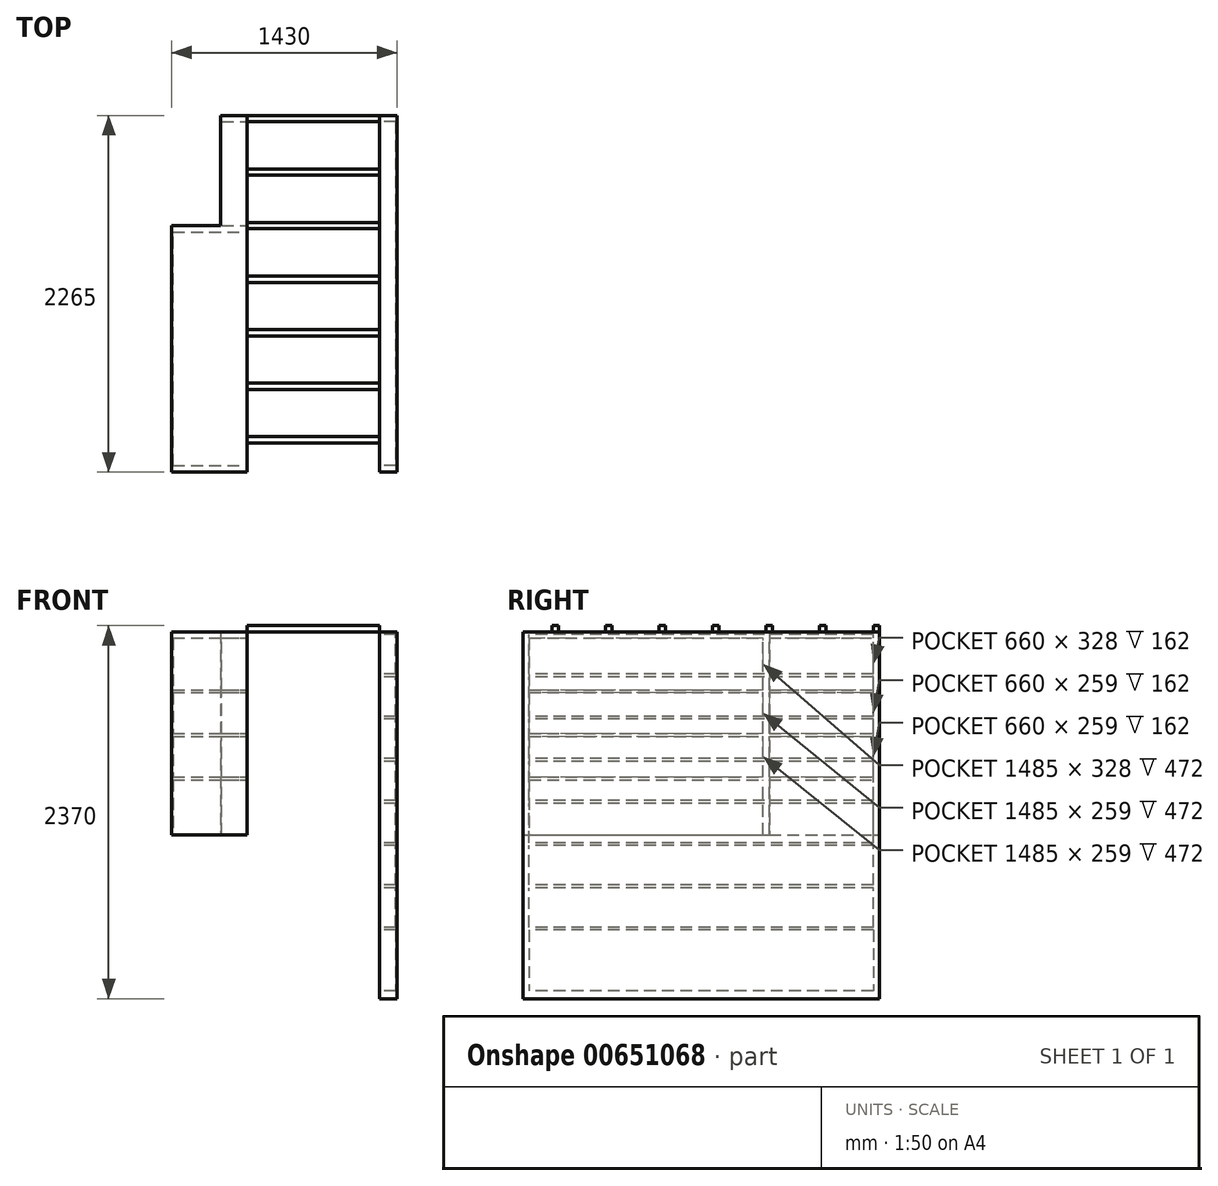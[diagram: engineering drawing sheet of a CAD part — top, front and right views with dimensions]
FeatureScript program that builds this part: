
annotation { "Feature Type Name" : "Feature", "Feature Type Description" : "" }
export const myFeature = defineFeature(function(context is Context, id is Id, definition is map)
    precondition{}
    {
        {
            var Q0;
            Q0=qCreatedBy(makeId("Top.planeOp"),FACE);
            var sketch = newSketch(context, id + "F0", { "sketchPlane" : qUnion([Q0])});
            skLineSegment(sketch, "E0.bottom", {"start": v(0, 0) * mm, "end": v(-110, 0) * mm});
            skLineSegment(sketch, "E0.left", {"start": v(0, 0) * mm, "end": v(0, 789.64) * mm});
            skLineSegment(sketch, "E0.right", {"start": v(-110, 0) * mm, "end": v(-110, 789.64) * mm});
            skLineSegment(sketch, "E1.bottom", {"start": v(-1120, 2265) * mm, "end": v(-950, 2265) * mm});
            skLineSegment(sketch, "E1.top", {"start": v(-1120, 0) * mm, "end": v(-950, 0) * mm});
            skLineSegment(sketch, "E1.left", {"start": v(-1120, 2265) * mm, "end": v(-1120, 1565) * mm});
            skLineSegment(sketch, "E1.right", {"start": v(-950, 2265) * mm, "end": v(-950, 0) * mm});
            skLineSegment(sketch, "E2.bottom", {"start": v(-1120, 1565) * mm, "end": v(-1430, 1565) * mm});
            skLineSegment(sketch, "E2.top", {"start": v(-950, 0) * mm, "end": v(-1430, 0) * mm});
            skLineSegment(sketch, "E2.right", {"start": v(-1430, 1565) * mm, "end": v(-1430, 0) * mm});
            skLineSegment(sketch, "E3.bottom", {"start": v(-110, 2265) * mm, "end": v(0, 2265) * mm});
            skLineSegment(sketch, "E3.top", {"start": v(-110, 0) * mm, "end": v(0, 0) * mm});
            skLineSegment(sketch, "E3.left", {"start": v(-110, 2265) * mm, "end": v(-110, 0) * mm});
            skLineSegment(sketch, "E3.right", {"start": v(0, 2265) * mm, "end": v(0, 0) * mm});
            skSolve(sketch);
        }
        {
            var Q0;
            Q0=qSketchRegion(id+"F0",true);
            extrude(context, id + "F1", {"entities" : qUnion([Q0]), "depth" : 2330 * mm, "offsetDistance" : 25 * mm});
        }
        {
            var Q0;
            Q0=makeQuery(id+"F1.opExtrude","SWEPT_FACE",FACE,{"disambiguationData":[OSD([sQuery(id+"F0.wireOp",EDGE,"E3.left")])]});
            var sketch = newSketch(context, id + "F2", { "sketchPlane" : qUnion([Q0])});
            skLineSegment(sketch, "E4.0", {"start": v(-2265, 2330) * mm, "end": v(-2265, 0) * mm});
            skLineSegment(sketch, "E5.0", {"start": v(0, 2330) * mm, "end": v(0, 0) * mm});
            skLineSegment(sketch, "E6.0", {"start": v(-2265, 2330) * mm, "end": v(0, 2330) * mm});
            skLineSegment(sketch, "E7.0", {"start": v(-2265, 0) * mm, "end": v(0, 0) * mm});
            skLineSegment(sketch, "E8.bottom", {"start": v(-2225, 436) * mm, "end": v(-40, 436) * mm});
            skLineSegment(sketch, "E8.top", {"start": v(-2225, 50) * mm, "end": v(-40, 50) * mm});
            skLineSegment(sketch, "E8.left", {"start": v(-2225, 436) * mm, "end": v(-2225, 50) * mm});
            skLineSegment(sketch, "E8.right", {"start": v(-40, 436) * mm, "end": v(-40, 50) * mm});
            skLineSegment(sketch, "E9.bottom", {"start": v(-2225, 454) * mm, "end": v(-40, 454) * mm});
            skLineSegment(sketch, "E9.top", {"start": v(-2225, 704) * mm, "end": v(-40, 704) * mm});
            skLineSegment(sketch, "E9.left", {"start": v(-2225, 454) * mm, "end": v(-2225, 704) * mm});
            skLineSegment(sketch, "E9.right", {"start": v(-40, 454) * mm, "end": v(-40, 704) * mm});
            skLineSegment(sketch, "E10.bottom", {"start": v(-2225, 722) * mm, "end": v(-40, 722) * mm});
            skLineSegment(sketch, "E10.top", {"start": v(-2225, 972) * mm, "end": v(-40, 972) * mm});
            skLineSegment(sketch, "E10.left", {"start": v(-2225, 722) * mm, "end": v(-2225, 972) * mm});
            skLineSegment(sketch, "E10.right", {"start": v(-40, 722) * mm, "end": v(-40, 972) * mm});
            skLineSegment(sketch, "E11.bottom", {"start": v(-2225, 990) * mm, "end": v(-40, 990) * mm});
            skLineSegment(sketch, "E11.top", {"start": v(-2225, 1240) * mm, "end": v(-40, 1240) * mm});
            skLineSegment(sketch, "E11.left", {"start": v(-2225, 990) * mm, "end": v(-2225, 1240) * mm});
            skLineSegment(sketch, "E11.right", {"start": v(-40, 990) * mm, "end": v(-40, 1240) * mm});
            skLineSegment(sketch, "E12.bottom", {"start": v(-2225, 1258) * mm, "end": v(-40, 1258) * mm});
            skLineSegment(sketch, "E12.top", {"start": v(-2225, 1508) * mm, "end": v(-40, 1508) * mm});
            skLineSegment(sketch, "E12.left", {"start": v(-2225, 1258) * mm, "end": v(-2225, 1508) * mm});
            skLineSegment(sketch, "E12.right", {"start": v(-40, 1258) * mm, "end": v(-40, 1508) * mm});
            skLineSegment(sketch, "E13.bottom", {"start": v(-2225, 1526) * mm, "end": v(-40, 1526) * mm});
            skLineSegment(sketch, "E13.top", {"start": v(-2225, 1776) * mm, "end": v(-40, 1776) * mm});
            skLineSegment(sketch, "E13.left", {"start": v(-2225, 1526) * mm, "end": v(-2225, 1776) * mm});
            skLineSegment(sketch, "E13.right", {"start": v(-40, 1526) * mm, "end": v(-40, 1776) * mm});
            skLineSegment(sketch, "E14.bottom", {"start": v(-2225, 1794) * mm, "end": v(-40, 1794) * mm});
            skLineSegment(sketch, "E14.top", {"start": v(-2225, 2044) * mm, "end": v(-40, 2044) * mm});
            skLineSegment(sketch, "E14.left", {"start": v(-2225, 1794) * mm, "end": v(-2225, 2044) * mm});
            skLineSegment(sketch, "E14.right", {"start": v(-40, 1794) * mm, "end": v(-40, 2044) * mm});
            skLineSegment(sketch, "E15.bottom", {"start": v(-2225, 2062) * mm, "end": v(-40, 2062) * mm});
            skLineSegment(sketch, "E15.top", {"start": v(-2225, 2312) * mm, "end": v(-40, 2312) * mm});
            skLineSegment(sketch, "E15.left", {"start": v(-2225, 2062) * mm, "end": v(-2225, 2312) * mm});
            skLineSegment(sketch, "E15.right", {"start": v(-40, 2062) * mm, "end": v(-40, 2312) * mm});
            skSolve(sketch);
        }
        {
            var Q0;
            Q0=makeQuery(id+"F2.imprint","IMPRINT",FACE,{"disambiguationData":[TD([[makeQuery(id+"F2.imprint","IMPRINT",EDGE,{"derivedFrom":sQuery(id+"F2.wireOp",EDGE,"E15.bottom")}),1.0]])]});
            var Q1;
            Q1=makeQuery(id+"F2.imprint","IMPRINT",FACE,{"disambiguationData":[TD([[makeQuery(id+"F2.imprint","IMPRINT",EDGE,{"derivedFrom":sQuery(id+"F2.wireOp",EDGE,"E14.bottom")}),1.0]])]});
            var Q2;
            Q2=makeQuery(id+"F2.imprint","IMPRINT",FACE,{"disambiguationData":[TD([[makeQuery(id+"F2.imprint","IMPRINT",EDGE,{"derivedFrom":sQuery(id+"F2.wireOp",EDGE,"E13.bottom")}),1.0]])]});
            var Q3;
            Q3=makeQuery(id+"F2.imprint","IMPRINT",FACE,{"disambiguationData":[TD([[makeQuery(id+"F2.imprint","IMPRINT",EDGE,{"derivedFrom":sQuery(id+"F2.wireOp",EDGE,"E12.bottom")}),1.0]])]});
            var Q4;
            Q4=makeQuery(id+"F2.imprint","IMPRINT",FACE,{"disambiguationData":[TD([[makeQuery(id+"F2.imprint","IMPRINT",EDGE,{"derivedFrom":sQuery(id+"F2.wireOp",EDGE,"E11.bottom")}),1.0]])]});
            var Q5;
            Q5=makeQuery(id+"F2.imprint","IMPRINT",FACE,{"disambiguationData":[TD([[makeQuery(id+"F2.imprint","IMPRINT",EDGE,{"derivedFrom":sQuery(id+"F2.wireOp",EDGE,"E10.bottom")}),1.0]])]});
            var Q6;
            Q6=makeQuery(id+"F2.imprint","IMPRINT",FACE,{"disambiguationData":[TD([[makeQuery(id+"F2.imprint","IMPRINT",EDGE,{"derivedFrom":sQuery(id+"F2.wireOp",EDGE,"E9.bottom")}),1.0]])]});
            var Q7;
            Q7=makeQuery(id+"F2.imprint","IMPRINT",FACE,{"disambiguationData":[TD([[makeQuery(id+"F2.imprint","IMPRINT",EDGE,{"derivedFrom":sQuery(id+"F2.wireOp",EDGE,"E8.bottom")}),-1.0]])]});
            extrude(context, id + "F3", {"entities" : qUnion([Q0, Q1, Q2, Q3, Q4, Q5, Q6, Q7]), "operationType" : NewBodyOperationType.REMOVE, "oppositeDirection" : true, "depth" : 102 * mm, "offsetDistance" : 25 * mm});
        }
        {
            var Q0;
            Q0=makeQuery(id+"F1.opExtrude","SWEPT_FACE",FACE,{"disambiguationData":[OSD([sQuery(id+"F0.wireOp",EDGE,"E1.right")])]});
            var sketch = newSketch(context, id + "F4", { "sketchPlane" : qUnion([Q0])});
            skLineSegment(sketch, "E16.0", {"start": v(0, 2330) * mm, "end": v(0, 0) * mm});
            skLineSegment(sketch, "E17.0.1", {"start": v(0, 0) * mm, "end": v(1565, 0) * mm});
            skLineSegment(sketch, "E17.0.3", {"start": v(1565, 0) * mm, "end": v(2265, 0) * mm});
            skLineSegment(sketch, "E17.0.5", {"start": v(2265, 0) * mm, "end": v(0, 0) * mm});
            skLineSegment(sketch, "E18.0", {"start": v(2265, 2330) * mm, "end": v(2265, 0) * mm});
            skLineSegment(sketch, "E19.bottom", {"start": v(0, 0) * mm, "end": v(2265, 0) * mm});
            skLineSegment(sketch, "E19.top", {"start": v(0, 1040) * mm, "end": v(2265, 1040) * mm});
            skLineSegment(sketch, "E19.left", {"start": v(0, 0) * mm, "end": v(0, 1040) * mm});
            skLineSegment(sketch, "E19.right", {"start": v(2265, 0) * mm, "end": v(2265, 1040) * mm});
            skSolve(sketch);
        }
        {
            var Q0;
            Q0=qSketchRegion(id+"F4",true);
            extrude(context, id + "F5", {"entities" : qUnion([Q0]), "operationType" : NewBodyOperationType.REMOVE, "oppositeDirection" : true, "depth" : 480 * mm, "offsetDistance" : 25 * mm});
        }
        {
            var Q0;
            Q0=makeQuery(id+"F1.opExtrude","SWEPT_FACE",FACE,{"disambiguationData":[OSD([sQuery(id+"F0.wireOp",EDGE,"E1.right")])]});
            var sketch = newSketch(context, id + "F6", { "sketchPlane" : qUnion([Q0])});
            skLineSegment(sketch, "E20.0", {"start": v(0, 2330) * mm, "end": v(0, 1040) * mm});
            skLineSegment(sketch, "E21.0", {"start": v(0, 1040) * mm, "end": v(2265, 1040) * mm});
            skLineSegment(sketch, "E22.0", {"start": v(2265, 2330) * mm, "end": v(2265, 1040) * mm});
            skLineSegment(sketch, "E23.bottom", {"start": v(2265, 1040) * mm, "end": v(2225, 1040) * mm});
            skLineSegment(sketch, "E23.top", {"start": v(2265, 2330) * mm, "end": v(2225, 2330) * mm});
            skLineSegment(sketch, "E23.left", {"start": v(2265, 1040) * mm, "end": v(2265, 2330) * mm});
            skLineSegment(sketch, "E23.right", {"start": v(2225, 1040) * mm, "end": v(2225, 2330) * mm});
            skLineSegment(sketch, "E24.bottom", {"start": v(0, 2290) * mm, "end": v(2225, 2290) * mm});
            skLineSegment(sketch, "E24.top", {"start": v(0, 2330) * mm, "end": v(2225, 2330) * mm});
            skLineSegment(sketch, "E24.left", {"start": v(0, 2290) * mm, "end": v(0, 2330) * mm});
            skLineSegment(sketch, "E24.right", {"start": v(2225, 2290) * mm, "end": v(2225, 2330) * mm});
            skLineSegment(sketch, "E25.bottom", {"start": v(0, 2290) * mm, "end": v(40, 2290) * mm});
            skLineSegment(sketch, "E25.top", {"start": v(0, 1040) * mm, "end": v(40, 1040) * mm});
            skLineSegment(sketch, "E25.left", {"start": v(0, 2290) * mm, "end": v(0, 1040) * mm});
            skLineSegment(sketch, "E25.right", {"start": v(40, 2290) * mm, "end": v(40, 1040) * mm});
            skLineSegment(sketch, "E26.bottom", {"start": v(1565, 1040) * mm, "end": v(1525, 1040) * mm});
            skLineSegment(sketch, "E26.top", {"start": v(1565, 2290) * mm, "end": v(1525, 2290) * mm});
            skLineSegment(sketch, "E26.left", {"start": v(1565, 1040) * mm, "end": v(1565, 2290) * mm});
            skLineSegment(sketch, "E26.right", {"start": v(1525, 1040) * mm, "end": v(1525, 2290) * mm});
            skLineSegment(sketch, "E27.bottom", {"start": v(40, 1390) * mm, "end": v(2225, 1390) * mm});
            skLineSegment(sketch, "E27.top", {"start": v(40, 1408) * mm, "end": v(2225, 1408) * mm});
            skLineSegment(sketch, "E27.left", {"start": v(40, 1390) * mm, "end": v(40, 1408) * mm});
            skLineSegment(sketch, "E27.right", {"start": v(2225, 1390) * mm, "end": v(2225, 1408) * mm});
            skLineSegment(sketch, "E28.bottom", {"start": v(40, 1667) * mm, "end": v(2225, 1667) * mm});
            skLineSegment(sketch, "E28.top", {"start": v(40, 1685) * mm, "end": v(2225, 1685) * mm});
            skLineSegment(sketch, "E28.left", {"start": v(40, 1667) * mm, "end": v(40, 1685) * mm});
            skLineSegment(sketch, "E28.right", {"start": v(2225, 1667) * mm, "end": v(2225, 1685) * mm});
            skLineSegment(sketch, "E29.bottom", {"start": v(40, 1944) * mm, "end": v(2225, 1944) * mm});
            skLineSegment(sketch, "E29.top", {"start": v(40, 1962) * mm, "end": v(2225, 1962) * mm});
            skLineSegment(sketch, "E29.left", {"start": v(40, 1944) * mm, "end": v(40, 1962) * mm});
            skLineSegment(sketch, "E29.right", {"start": v(2225, 1944) * mm, "end": v(2225, 1962) * mm});
            skSolve(sketch);
        }
        {
            var Q0;
            {var subQ3=sQuery(id+"F6.wireOp",EDGE,"E26.left");var subQ5=sQuery(id+"F6.wireOp",EDGE,"E27.bottom");var subQ7=makeQuery(id+"F6.imprint","INTERSECT",VERTEX,{"derivedFrom":[subQ3,subQ5]});Q0=makeQuery(id+"F6.imprint","IMPRINT",FACE,{"disambiguationData":[TD([[makeQuery(id+"F6.imprint","IMPRINT",EDGE,{"disambiguationData":[TD([[subQ7,1.0]])],"derivedFrom":subQ3}),-1.0]])]});}
            var Q1;
            {var subQ0=sQuery(id+"F6.wireOp",EDGE,"E27.top");var subQ5=sQuery(id+"F6.wireOp",EDGE,"E26.left");var subQ6=makeQuery(id+"F6.imprint","INTERSECT",VERTEX,{"derivedFrom":[subQ5,subQ0]});Q1=makeQuery(id+"F6.imprint","IMPRINT",FACE,{"disambiguationData":[TD([[makeQuery(id+"F6.imprint","IMPRINT",EDGE,{"disambiguationData":[TD([[subQ6,-1.0]])],"derivedFrom":subQ5}),-1.0]])]});}
            var Q2;
            {var subQ0=sQuery(id+"F6.wireOp",EDGE,"E28.top");var subQ5=sQuery(id+"F6.wireOp",EDGE,"E26.left");var subQ6=makeQuery(id+"F6.imprint","INTERSECT",VERTEX,{"derivedFrom":[subQ5,subQ0]});Q2=makeQuery(id+"F6.imprint","IMPRINT",FACE,{"disambiguationData":[TD([[makeQuery(id+"F6.imprint","IMPRINT",EDGE,{"disambiguationData":[TD([[subQ6,-1.0]])],"derivedFrom":subQ5}),-1.0]])]});}
            var Q3;
            {var subQ3=sQuery(id+"F6.wireOp",EDGE,"E29.top");var subQ5=sQuery(id+"F6.wireOp",EDGE,"E26.left");var subQ6=makeQuery(id+"F6.imprint","INTERSECT",VERTEX,{"derivedFrom":[subQ5,subQ3]});Q3=makeQuery(id+"F6.imprint","IMPRINT",FACE,{"disambiguationData":[TD([[makeQuery(id+"F6.imprint","IMPRINT",EDGE,{"disambiguationData":[TD([[subQ6,-1.0]])],"derivedFrom":subQ5}),-1.0]])]});}
            extrude(context, id + "F7", {"entities" : qUnion([Q0, Q1, Q2, Q3]), "operationType" : NewBodyOperationType.REMOVE, "oppositeDirection" : true, "depth" : 162 * mm, "offsetDistance" : 25 * mm});
        }
        {
            var Q0;
            {var subQ3=sQuery(id+"F6.wireOp",EDGE,"E26.right");var subQ5=sQuery(id+"F6.wireOp",EDGE,"E27.bottom");var subQ7=makeQuery(id+"F6.imprint","INTERSECT",VERTEX,{"derivedFrom":[subQ3,subQ5]});Q0=makeQuery(id+"F6.imprint","IMPRINT",FACE,{"disambiguationData":[TD([[makeQuery(id+"F6.imprint","IMPRINT",EDGE,{"disambiguationData":[TD([[subQ7,1.0]])],"derivedFrom":subQ3}),1.0]])]});}
            var Q1;
            {var subQ0=sQuery(id+"F6.wireOp",EDGE,"E27.top");var subQ5=sQuery(id+"F6.wireOp",EDGE,"E26.right");var subQ6=makeQuery(id+"F6.imprint","INTERSECT",VERTEX,{"derivedFrom":[subQ5,subQ0]});Q1=makeQuery(id+"F6.imprint","IMPRINT",FACE,{"disambiguationData":[TD([[makeQuery(id+"F6.imprint","IMPRINT",EDGE,{"disambiguationData":[TD([[subQ6,-1.0]])],"derivedFrom":subQ5}),1.0]])]});}
            var Q2;
            {var subQ0=sQuery(id+"F6.wireOp",EDGE,"E28.top");var subQ5=sQuery(id+"F6.wireOp",EDGE,"E26.right");var subQ6=makeQuery(id+"F6.imprint","INTERSECT",VERTEX,{"derivedFrom":[subQ5,subQ0]});Q2=makeQuery(id+"F6.imprint","IMPRINT",FACE,{"disambiguationData":[TD([[makeQuery(id+"F6.imprint","IMPRINT",EDGE,{"disambiguationData":[TD([[subQ6,-1.0]])],"derivedFrom":subQ5}),1.0]])]});}
            var Q3;
            {var subQ3=sQuery(id+"F6.wireOp",EDGE,"E26.right");var subQ5=sQuery(id+"F6.wireOp",EDGE,"E29.top");var subQ7=makeQuery(id+"F6.imprint","INTERSECT",VERTEX,{"derivedFrom":[subQ3,subQ5]});Q3=makeQuery(id+"F6.imprint","IMPRINT",FACE,{"disambiguationData":[TD([[makeQuery(id+"F6.imprint","IMPRINT",EDGE,{"disambiguationData":[TD([[subQ7,-1.0]])],"derivedFrom":subQ3}),1.0]])]});}
            extrude(context, id + "F8", {"entities" : qUnion([Q0, Q1, Q2, Q3]), "operationType" : NewBodyOperationType.REMOVE, "oppositeDirection" : true, "depth" : 472 * mm, "offsetDistance" : 25 * mm});
        }
        {
            var Q0;
            Q0=makeQuery(id+"F1.opExtrude","CAP_FACE",FACE,{"disambiguationData":[OSD([sQuery(id+"F0.wireOp",EDGE,"E1.bottom"),sQuery(id+"F0.wireOp",EDGE,"E1.left"),sQuery(id+"F0.wireOp",EDGE,"E1.right"),sQuery(id+"F0.wireOp",EDGE,"E2.bottom"),sQuery(id+"F0.wireOp",EDGE,"E2.top"),sQuery(id+"F0.wireOp",EDGE,"E2.right")])],"isStart":false});
            var sketch = newSketch(context, id + "F9", { "sketchPlane" : qUnion([Q0])});
            skLineSegment(sketch, "E30.0", {"start": v(-950, 0) * mm, "end": v(-950, 2225) * mm});
            skLineSegment(sketch, "E31.0.0", {"start": v(-110, 2265) * mm, "end": v(-110, 0) * mm});
            skLineSegment(sketch, "E31.0.1", {"start": v(-110, 0) * mm, "end": v(0, 0) * mm});
            skLineSegment(sketch, "E31.0.2", {"start": v(0, 0) * mm, "end": v(0, 2265) * mm});
            skLineSegment(sketch, "E31.0.3", {"start": v(0, 2265) * mm, "end": v(-110, 2265) * mm});
            skLineSegment(sketch, "E32.0", {"start": v(-950, 0) * mm, "end": v(-1430, 0) * mm});
            skLineSegment(sketch, "E33.0", {"start": v(-950, 2265) * mm, "end": v(-950, 2225) * mm});
            skLineSegment(sketch, "E34.0", {"start": v(-1120, 2265) * mm, "end": v(-950, 2265) * mm});
            skLineSegment(sketch, "E35.bottom", {"start": v(-950, 565) * mm, "end": v(-110, 565) * mm});
            skLineSegment(sketch, "E35.top", {"start": v(-950, 525) * mm, "end": v(-110, 525) * mm});
            skLineSegment(sketch, "E35.left", {"start": v(-950, 565) * mm, "end": v(-950, 525) * mm});
            skLineSegment(sketch, "E35.right", {"start": v(-110, 565) * mm, "end": v(-110, 525) * mm});
            skLineSegment(sketch, "E36.bottom", {"start": v(-950, 905) * mm, "end": v(-110, 905) * mm});
            skLineSegment(sketch, "E36.top", {"start": v(-950, 865) * mm, "end": v(-110, 865) * mm});
            skLineSegment(sketch, "E36.left", {"start": v(-950, 905) * mm, "end": v(-950, 865) * mm});
            skLineSegment(sketch, "E36.right", {"start": v(-110, 905) * mm, "end": v(-110, 865) * mm});
            skLineSegment(sketch, "E37.bottom", {"start": v(-950, 1245) * mm, "end": v(-110, 1245) * mm});
            skLineSegment(sketch, "E37.top", {"start": v(-950, 1205) * mm, "end": v(-110, 1205) * mm});
            skLineSegment(sketch, "E37.left", {"start": v(-950, 1245) * mm, "end": v(-950, 1205) * mm});
            skLineSegment(sketch, "E37.right", {"start": v(-110, 1245) * mm, "end": v(-110, 1205) * mm});
            skLineSegment(sketch, "E38.bottom", {"start": v(-950, 1545) * mm, "end": v(-110, 1545) * mm});
            skLineSegment(sketch, "E38.top", {"start": v(-950, 1585) * mm, "end": v(-110, 1585) * mm});
            skLineSegment(sketch, "E38.left", {"start": v(-950, 1545) * mm, "end": v(-950, 1585) * mm});
            skLineSegment(sketch, "E38.right", {"start": v(-110, 1545) * mm, "end": v(-110, 1585) * mm});
            skLineSegment(sketch, "E39.bottom", {"start": v(-950, 1885) * mm, "end": v(-110, 1885) * mm});
            skLineSegment(sketch, "E39.top", {"start": v(-950, 1925) * mm, "end": v(-110, 1925) * mm});
            skLineSegment(sketch, "E39.left", {"start": v(-950, 1885) * mm, "end": v(-950, 1925) * mm});
            skLineSegment(sketch, "E39.right", {"start": v(-110, 1885) * mm, "end": v(-110, 1925) * mm});
            skLineSegment(sketch, "E40.bottom", {"start": v(-950, 2225) * mm, "end": v(-110, 2225) * mm});
            skLineSegment(sketch, "E40.top", {"start": v(-950, 2265) * mm, "end": v(-110, 2265) * mm});
            skLineSegment(sketch, "E40.left", {"start": v(-950, 2225) * mm, "end": v(-950, 2265) * mm});
            skLineSegment(sketch, "E40.right", {"start": v(-110, 2225) * mm, "end": v(-110, 2265) * mm});
            skLineSegment(sketch, "E41.bottom", {"start": v(-950, 0) * mm, "end": v(-110, 0) * mm});
            skLineSegment(sketch, "E41.top", {"start": v(-950, 225) * mm, "end": v(-110, 225) * mm});
            skLineSegment(sketch, "E41.left", {"start": v(-950, 0) * mm, "end": v(-950, 225) * mm});
            skLineSegment(sketch, "E41.right", {"start": v(-110, 0) * mm, "end": v(-110, 225) * mm});
            skLineSegment(sketch, "E42.top", {"start": v(-950, 185) * mm, "end": v(-110, 185) * mm});
            skLineSegment(sketch, "E42.left", {"start": v(-950, 225) * mm, "end": v(-950, 185) * mm});
            skLineSegment(sketch, "E42.right", {"start": v(-110, 225) * mm, "end": v(-110, 185) * mm});
            skLineSegment(sketch, "E43.bottom", {"start": v(-950, 2265) * mm, "end": v(-990, 2265) * mm});
            skLineSegment(sketch, "E43.top", {"start": v(-950, 185) * mm, "end": v(-990, 185) * mm});
            skLineSegment(sketch, "E43.left", {"start": v(-950, 2265) * mm, "end": v(-950, 185) * mm});
            skLineSegment(sketch, "E43.right", {"start": v(-990, 2265) * mm, "end": v(-990, 185) * mm});
            skLineSegment(sketch, "E44.bottom", {"start": v(-110, 2265) * mm, "end": v(-70, 2265) * mm});
            skLineSegment(sketch, "E44.top", {"start": v(-110, 185) * mm, "end": v(-70, 185) * mm});
            skLineSegment(sketch, "E44.left", {"start": v(-110, 2265) * mm, "end": v(-110, 185) * mm});
            skLineSegment(sketch, "E44.right", {"start": v(-70, 2265) * mm, "end": v(-70, 185) * mm});
            skSolve(sketch);
        }
        {
            var Q0;
            {var subQ0=sQuery(id+"F9.wireOp",EDGE,"E39.bottom");Q0=makeQuery(id+"F9.imprint","IMPRINT",FACE,{"disambiguationData":[TD([[makeQuery(id+"F9.imprint","IMPRINT",EDGE,{"derivedFrom":subQ0}),1.0]])]});}
            var Q1;
            {var subQ0=sQuery(id+"F9.wireOp",EDGE,"E38.bottom");Q1=makeQuery(id+"F9.imprint","IMPRINT",FACE,{"disambiguationData":[TD([[makeQuery(id+"F9.imprint","IMPRINT",EDGE,{"derivedFrom":subQ0}),1.0]])]});}
            var Q2;
            {var subQ0=sQuery(id+"F9.wireOp",EDGE,"E37.bottom");Q2=makeQuery(id+"F9.imprint","IMPRINT",FACE,{"disambiguationData":[TD([[makeQuery(id+"F9.imprint","IMPRINT",EDGE,{"derivedFrom":subQ0}),-1.0]])]});}
            var Q3;
            {var subQ0=sQuery(id+"F9.wireOp",EDGE,"E36.bottom");Q3=makeQuery(id+"F9.imprint","IMPRINT",FACE,{"disambiguationData":[TD([[makeQuery(id+"F9.imprint","IMPRINT",EDGE,{"derivedFrom":subQ0}),-1.0]])]});}
            var Q4;
            {var subQ0=sQuery(id+"F9.wireOp",EDGE,"E41.top");Q4=makeQuery(id+"F9.imprint","IMPRINT",FACE,{"disambiguationData":[TD([[makeQuery(id+"F9.imprint","IMPRINT",EDGE,{"derivedFrom":subQ0}),-1.0]])]});}
            var Q5;
            {var subQ0=sQuery(id+"F9.wireOp",EDGE,"E35.bottom");Q5=makeQuery(id+"F9.imprint","IMPRINT",FACE,{"disambiguationData":[TD([[makeQuery(id+"F9.imprint","IMPRINT",EDGE,{"derivedFrom":subQ0}),-1.0]])]});}
            var Q6;
            {var subQ8=sQuery(id+"F9.wireOp",EDGE,"E44.bottom");Q6=makeQuery(id+"F9.imprint","IMPRINT",FACE,{"disambiguationData":[TD([[makeQuery(id+"F9.imprint","IMPRINT",EDGE,{"derivedFrom":subQ8}),-1.0]])]});}
            var Q7;
            {var subQ8=sQuery(id+"F9.wireOp",EDGE,"E43.bottom");Q7=makeQuery(id+"F9.imprint","IMPRINT",FACE,{"disambiguationData":[TD([[makeQuery(id+"F9.imprint","IMPRINT",EDGE,{"derivedFrom":subQ8}),-1.0]])]});}
            var Q8;
            {var subQ0=sQuery(id+"F9.wireOp",EDGE,"E40.bottom");Q8=makeQuery(id+"F9.imprint","IMPRINT",FACE,{"disambiguationData":[TD([[makeQuery(id+"F9.imprint","IMPRINT",EDGE,{"derivedFrom":subQ0}),1.0]])]});}
            extrude(context, id + "F10", {"entities" : qUnion([Q0, Q1, Q2, Q3, Q4, Q5, Q6, Q7, Q8]), "depth" : 40 * mm, "offsetDistance" : 25 * mm});
        }
    });
